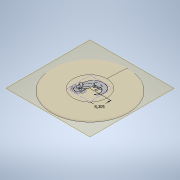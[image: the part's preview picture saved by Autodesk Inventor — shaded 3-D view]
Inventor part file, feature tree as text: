
AUTODESK INVENTOR PART (.ipt)
format: ipt  version: 2021 (Build 250183000, 183)  size: 367,104 bytes
history: native  units: mm
features: sketch x2, revolve x1, plane x1, other x1
ambient origin geometry x8: Origin, YZ Plane, XZ Plane, XY Plane, X Axis, Y Axis, Z Axis, Center Point
bodies: Volumenkörper1 (feature_tree)
feature tree (5):
  revolve  "Umdrehung1"
  plane  "Arbeitsebene2"
  sketch  "Skizze3"  dims[d2=0.0mm d3=0.4mm d4=2.0mm d5=2.0mm d6=12.0mm d7=90.0deg d8=2.0mm d11=8.305mm]
  sketch  "Skizze1"  dims[d0=25.0mm]
  other  "Bild1"
